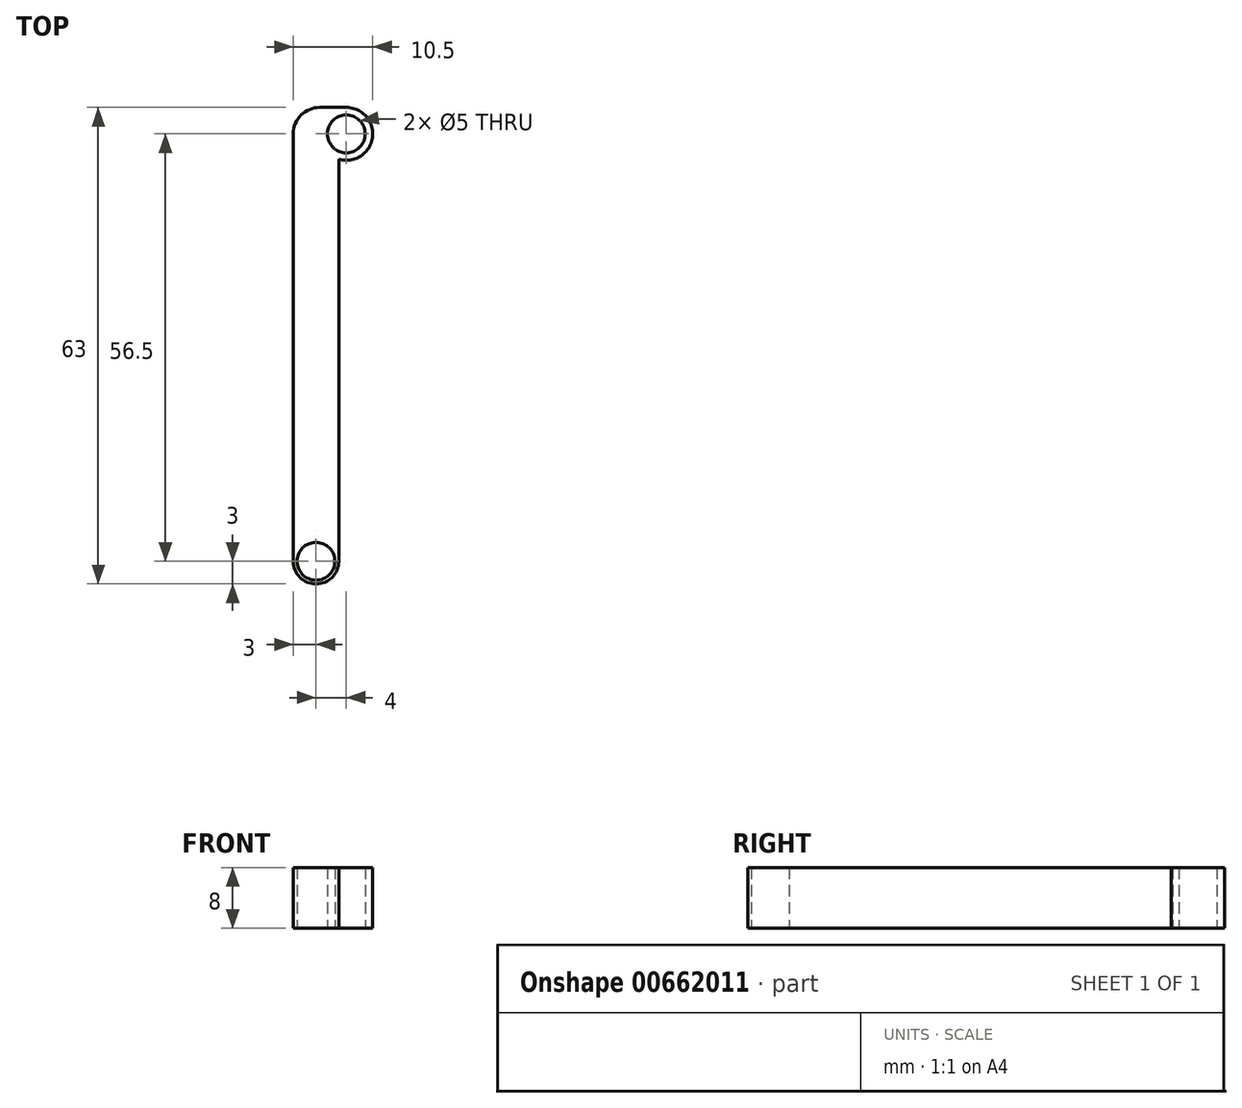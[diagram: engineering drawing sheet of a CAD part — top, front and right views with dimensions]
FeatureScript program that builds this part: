
annotation { "Feature Type Name" : "Feature", "Feature Type Description" : "" }
export const myFeature = defineFeature(function(context is Context, id is Id, definition is map)
    precondition{}
    {
        {
            var Q0;
            Q0=qCreatedBy(makeId("Top.planeOp"),FACE);
            var sketch = newSketch(context, id + "F0", { "sketchPlane" : qUnion([Q0])});
            skCircle(sketch, "E0", {"center": v(0, 0) * mm, "radius": 2.5 * mm});
            skArc(sketch, "E1", {"start": v(-7, -56.5) * mm, "mid": v(-4, -59.5) * mm, "end": v(-1, -56.5) * mm});
            skCircle(sketch, "E2", {"center": v(-4, -56.5) * mm, "radius": 2.5 * mm});
            skLineSegment(sketch, "E3", {"start": v(-1, -56.5) * mm, "end": v(-1, -3.35) * mm});
            skArc(sketch, "E4", {"start": v(0, 3.5) * mm, "mid": v(3.46, -0.5) * mm, "end": v(-1, -3.35) * mm});
            skLineSegment(sketch, "E5", {"start": v(-7, 0) * mm, "end": v(0, 0) * mm});
            skArc(sketch, "E6", {"start": v(-3.5, 3.5) * mm, "mid": v(-5.97, 2.47) * mm, "end": v(-7, 0) * mm});
            skLineSegment(sketch, "E7", {"start": v(-3.5, 3.5) * mm, "end": v(0, 3.5) * mm});
            skLineSegment(sketch, "E8", {"start": v(-7, -56.5) * mm, "end": v(-7, 0) * mm});
            skSolve(sketch);
        }
        {
            var Q0;
            Q0 = qSketchRegion(id + "F0", true);
            var Q1;
            Q1 = qBodyType(qCreatedBy(id + "F0" ,EDGE), BodyType.WIRE);
            extrude(context, id + "F1", {"entities" : qUnion([Q0]), "surfaceEntities" : qUnion([Q1]), "depth" : 8 * mm, "offsetDistance" : 25 * mm});
        }
    });
